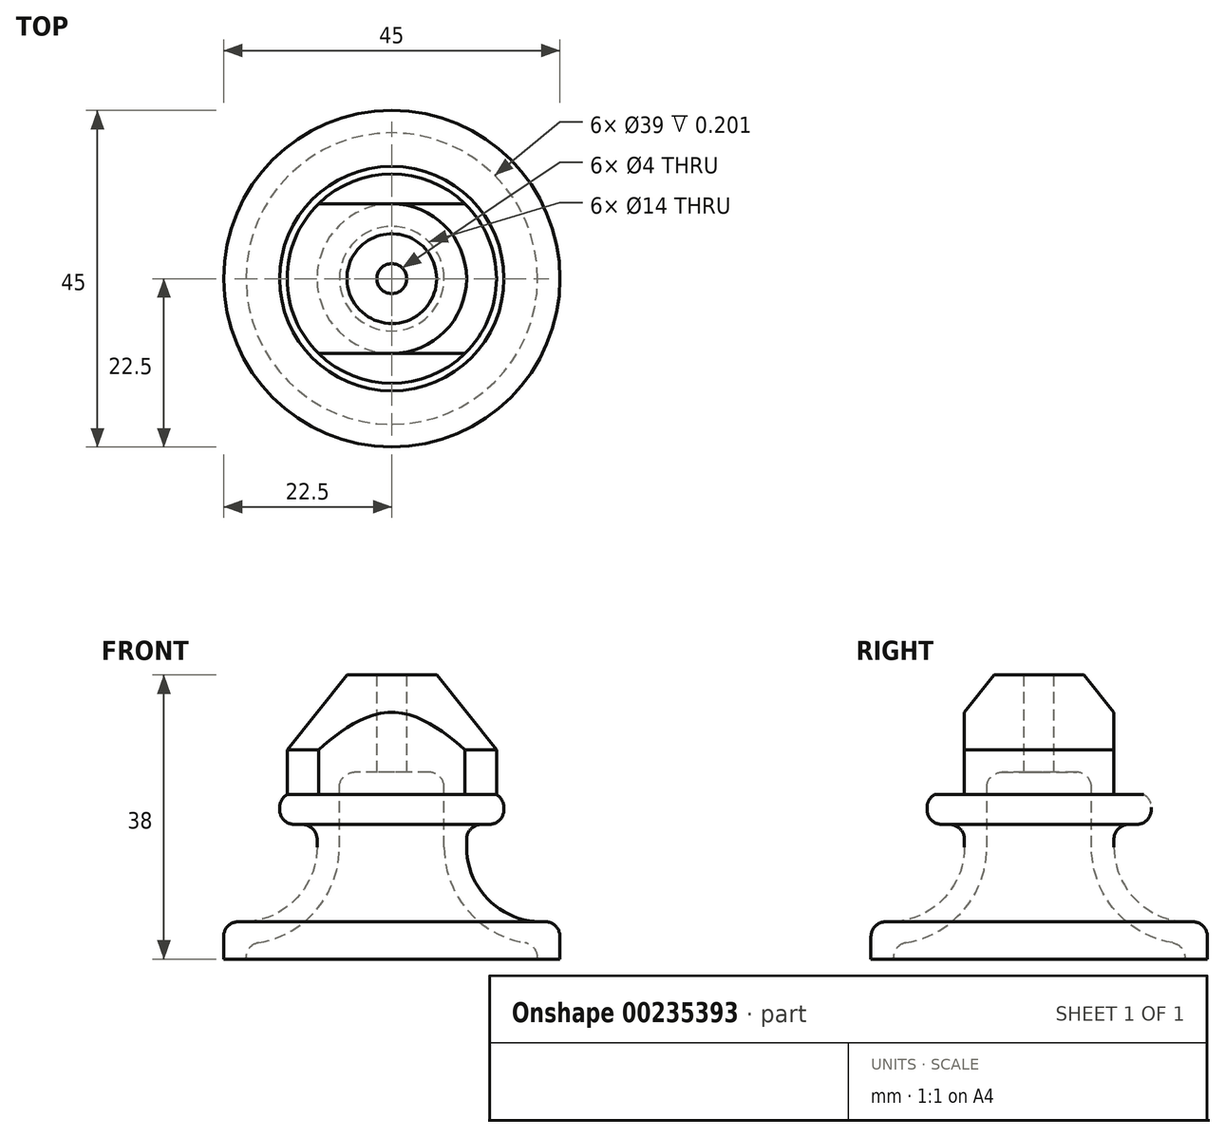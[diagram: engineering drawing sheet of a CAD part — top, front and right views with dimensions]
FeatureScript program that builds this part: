
annotation { "Feature Type Name" : "Feature", "Feature Type Description" : "" }
export const myFeature = defineFeature(function(context is Context, id is Id, definition is map)
    precondition{}
    {
        {
            var Q0;
            Q0=qCreatedBy(makeId("Front.planeOp"),FACE);
            var sketch = newSketch(context, id + "F0", { "sketchPlane" : qUnion([Q0])});
            skLineSegment(sketch, "E0", {"start": v(0, 0) * mm, "end": v(0, -30.22) * mm, "construction": true});
            skLineSegment(sketch, "E1", {"start": v(0, 0) * mm, "end": v(22.5, 0) * mm});
            skLineSegment(sketch, "E2", {"start": v(22.5, 0) * mm, "end": v(22.5, 3) * mm});
            skLineSegment(sketch, "E3", {"start": v(14, 22) * mm, "end": v(14, 28) * mm});
            skLineSegment(sketch, "E4", {"start": v(14, 28) * mm, "end": v(6, 38) * mm});
            skLineSegment(sketch, "E5", {"start": v(6, 38) * mm, "end": v(2, 38) * mm});
            skLineSegment(sketch, "E6", {"start": v(2, 25) * mm, "end": v(5, 25) * mm});
            skLineSegment(sketch, "E7", {"start": v(7, 23) * mm, "end": v(7, 15) * mm});
            skLineSegment(sketch, "E8", {"start": v(19.5, 2) * mm, "end": v(19.5, 0) * mm});
            skLineSegment(sketch, "E9", {"start": v(15, 20.27) * mm, "end": v(15, 20) * mm});
            skLineSegment(sketch, "E10", {"start": v(13, 18) * mm, "end": v(12, 18) * mm});
            skLineSegment(sketch, "E11", {"start": v(10, 16) * mm, "end": v(10, 15) * mm});
            skArc(sketch, "E12", {"start": v(10, 15) * mm, "mid": v(13.08, 7.77) * mm, "end": v(20.42, 5) * mm});
            skLineSegment(sketch, "E13", {"start": v(2, 38) * mm, "end": v(2, 25) * mm});
            skPoint(sketch, "E14.visualSharp", {"position": v(22.5, 5.3) * mm});
            skArc(sketch, "E14.filletArc", {"start": v(22.5, 3) * mm, "mid": v(21.88, 4.45) * mm, "end": v(20.42, 5) * mm});
            skPoint(sketch, "E15.visualSharp", {"position": v(10, 18) * mm});
            skArc(sketch, "E15.filletArc", {"start": v(12, 18) * mm, "mid": v(10.59, 17.41) * mm, "end": v(10, 16) * mm});
            skPoint(sketch, "E16.visualSharp", {"position": v(19.5, 3.31) * mm});
            skPoint(sketch, "E17.visualSharp", {"position": v(15, 18) * mm});
            skArc(sketch, "E17.filletArc", {"start": v(13, 18) * mm, "mid": v(14.41, 18.59) * mm, "end": v(15, 20) * mm});
            skPoint(sketch, "E18.visualSharp", {"position": v(15, 22) * mm});
            skArc(sketch, "E18.filletArc", {"start": v(15, 20.27) * mm, "mid": v(14.73, 21.27) * mm, "end": v(14, 22) * mm});
            skPoint(sketch, "E19.visualSharp", {"position": v(7, 25) * mm});
            skArc(sketch, "E19.filletArc", {"start": v(7, 23) * mm, "mid": v(6.41, 24.41) * mm, "end": v(5, 25) * mm});
            skPoint(sketch, "E20.orphan", {"position": v(0, 38) * mm});
            skPoint(sketch, "E21.orphan", {"position": v(0, 31.16) * mm});
            skArc(sketch, "E22.0", {"start": v(7, 15) * mm, "mid": v(10.63, 5.98) * mm, "end": v(19.5, 2) * mm});
            skSolve(sketch);
        }
        {
            var Q0;
            {var subQ0=sQuery(id+"F0.wireOp",EDGE,"E2");Q0=makeQuery(id+"F0.imprint","IMPRINT",FACE,{"disambiguationData":[TD([[makeQuery(id+"F0.imprint","IMPRINT",EDGE,{"derivedFrom":subQ0}),1.0]])]});}
            var Q1;
            Q1=sQuery(id+"F0.wireOp",EDGE,"E0");
            revolve(context, id + "F1", {"entities" : qUnion([Q0]), "axis" : qUnion([Q1]), "revolveType" : RevolveType.FULL});
        }
        {
            var Q0;
            Q0=makeQuery(id+"F1.opRevolve","SWEPT_EDGE",EDGE,{"disambiguationData":[OSD([sQuery(id+"F0.wireOp",EDGE,"E8"),sQuery(id+"F0.wireOp",EDGE,"E22.0")])]});
            var Q1;
            Q1=makeQuery(id+"F1.opRevolve","SWEPT_EDGE",EDGE,{"disambiguationData":[OSD([sQuery(id+"F0.wireOp",EDGE,"E6"),sQuery(id+"F0.wireOp",EDGE,"E19.filletArc")])]});
            fillet(context, id + "F2", {"entities" : qUnion([Q0, Q1]), "radius" : 2 * mm, "tangentPropagation" : true, "allowEdgeOverflow" : false});
        }
        {
            var Q0;
            Q0=makeQuery(id+"F1.opRevolve","SWEPT_FACE",FACE,{"disambiguationData":[OSD([sQuery(id+"F0.wireOp",EDGE,"E5")])]});
            var sketch = newSketch(context, id + "F3", { "sketchPlane" : qUnion([Q0])});
            skCircle(sketch, "E23.0", {"center": v(0, 0) * mm, "radius": 14 * mm});
            skLineSegment(sketch, "E24.bottom", {"start": v(9.8, 10) * mm, "end": v(-9.8, 10) * mm});
            skLineSegment(sketch, "E24.top", {"start": v(9.8, -10) * mm, "end": v(-9.8, -10) * mm});
            skLineSegment(sketch, "E24.left", {"start": v(9.8, 10) * mm, "end": v(9.8, -10) * mm});
            skLineSegment(sketch, "E24.right", {"start": v(-9.8, 10) * mm, "end": v(-9.8, -10) * mm});
            skSolve(sketch);
        }
        {
            var Q0;
            {var subQ0=sQuery(id+"F3.wireOp",EDGE,"E24.bottom");Q0=makeQuery(id+"F3.imprint","IMPRINT",FACE,{"disambiguationData":[TD([[makeQuery(id+"F3.imprint","IMPRINT",EDGE,{"derivedFrom":subQ0}),-1.0]])]});}
            var Q1;
            {var subQ0=sQuery(id+"F3.wireOp",EDGE,"E24.top");Q1=makeQuery(id+"F3.imprint","IMPRINT",FACE,{"disambiguationData":[TD([[makeQuery(id+"F3.imprint","IMPRINT",EDGE,{"derivedFrom":subQ0}),1.0]])]});}
            var Q2;
            Q2=makeQuery(id+"F1.opRevolve","SWEPT_FACE",FACE,{"disambiguationData":[OSD([sQuery(id+"F0.wireOp",EDGE,"E6")])]});
            extrude(context, id + "F4", {"entities" : qUnion([Q0, Q1]), "operationType" : NewBodyOperationType.REMOVE, "oppositeDirection" : true, "endBoundEntityFace" : qUnion([Q2]), "depth" : 16 * mm});
        }
    });
